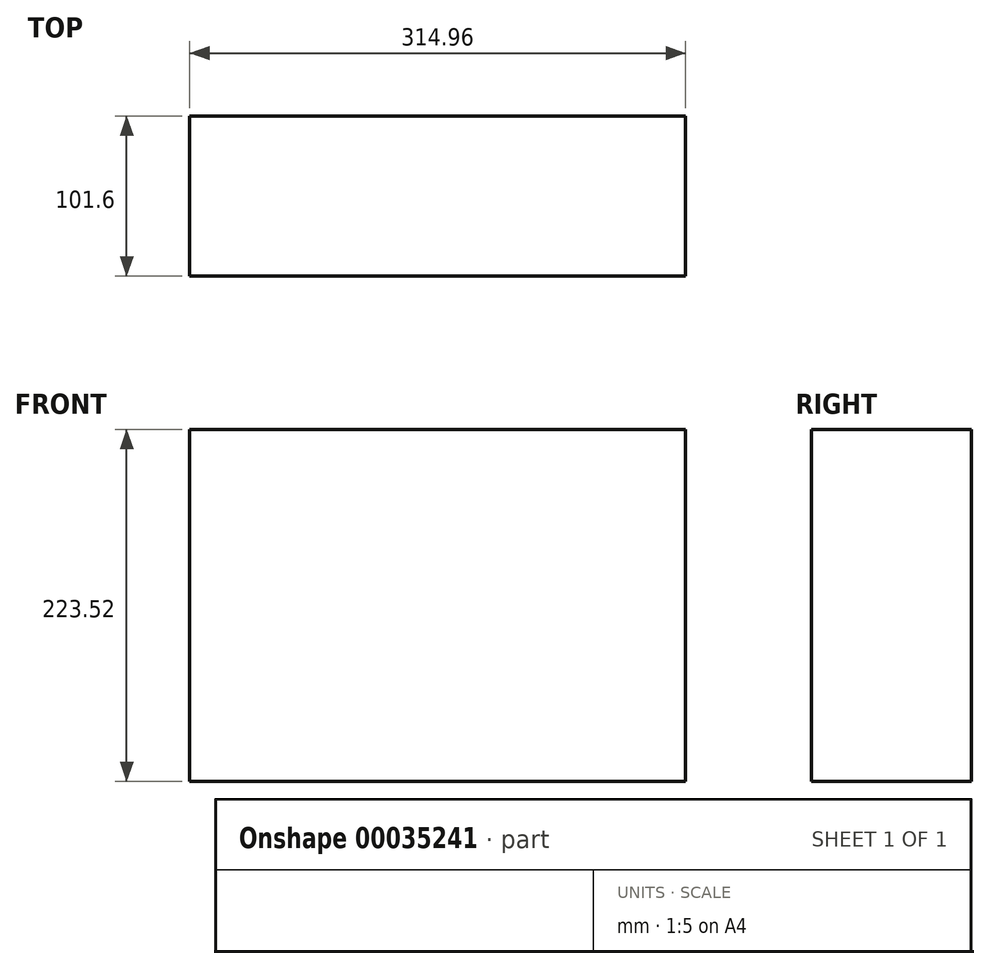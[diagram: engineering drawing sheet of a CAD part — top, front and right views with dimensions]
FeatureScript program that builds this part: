
annotation { "Feature Type Name" : "Feature", "Feature Type Description" : "" }
export const myFeature = defineFeature(function(context is Context, id is Id, definition is map)
    precondition{}
    {
        {
            var Q0;
            Q0=qCreatedBy(makeId("Front.planeOp"),FACE);
            var sketch = newSketch(context, id + "F0", { "sketchPlane" : qUnion([Q0])});
            skLineSegment(sketch, "E0.rect.bottom", {"start": v(157.48, -111.76) * mm, "end": v(-157.48, -111.76) * mm});
            skLineSegment(sketch, "E0.rect.top", {"start": v(157.48, 111.76) * mm, "end": v(-157.48, 111.76) * mm});
            skLineSegment(sketch, "E0.rect.left", {"start": v(157.48, -111.76) * mm, "end": v(157.48, 111.76) * mm});
            skLineSegment(sketch, "E0.rect.right", {"start": v(-157.48, -111.76) * mm, "end": v(-157.48, 111.76) * mm});
            skPoint(sketch, "E0.rect.middle", {"position": v(0, 0) * mm});
            skSolve(sketch);
        }
        {
            var Q0;
            Q0=makeQuery(id+"F0.imprint","IMPRINT",FACE,{"disambiguationData":[TD([[makeQuery(id+"F0.imprint","IMPRINT",EDGE,{"derivedFrom":sQuery(id+"F0.wireOp",EDGE,"E0.rect.bottom")}),-1.0]])]});
            extrude(context, id + "F1", {"entities" : qUnion([Q0]), "depth" : 101.6 * mm});
        }
    });
